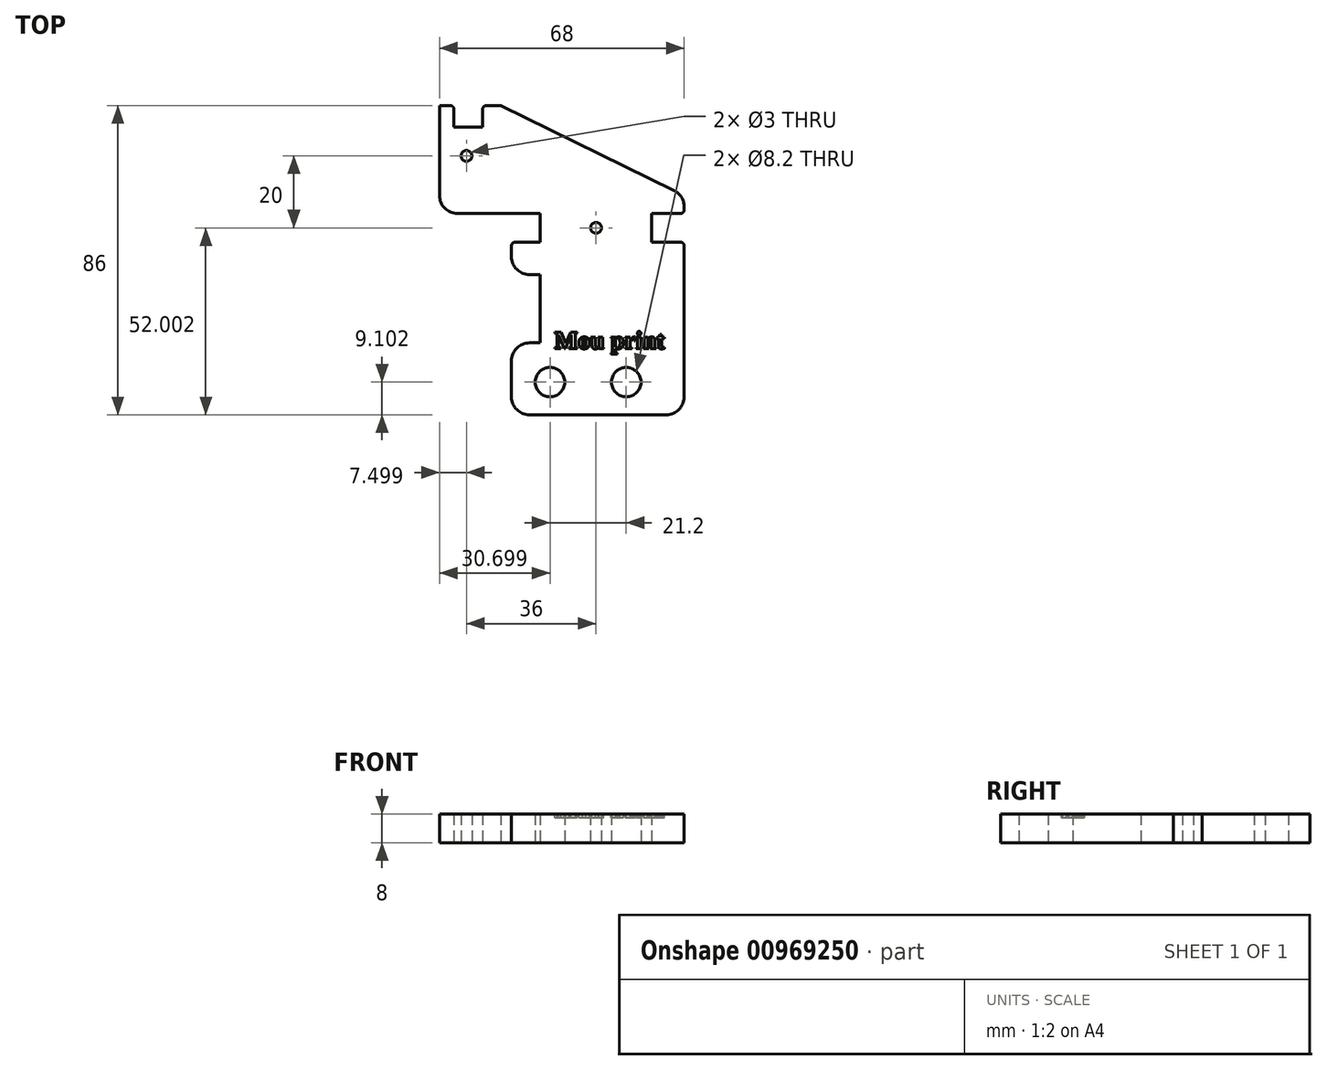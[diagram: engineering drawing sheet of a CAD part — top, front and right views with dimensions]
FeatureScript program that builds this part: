
annotation { "Feature Type Name" : "Feature", "Feature Type Description" : "" }
export const myFeature = defineFeature(function(context is Context, id is Id, definition is map)
    precondition{}
    {
        {
            var Q0;
            Q0=qCreatedBy(makeId("Top.planeOp"),FACE);
            var sketch = newSketch(context, id + "F0", { "sketchPlane" : qUnion([Q0])});
            skLineSegment(sketch, "E0", {"start": v(-27.53, -40.03) * mm, "end": v(10.47, -40.03) * mm});
            skLineSegment(sketch, "E1", {"start": v(-32.53, -35.03) * mm, "end": v(-32.53, -25.03) * mm});
            skLineSegment(sketch, "E2", {"start": v(-27.53, -20.03) * mm, "end": v(-24.53, -20.03) * mm});
            skLineSegment(sketch, "E3", {"start": v(-24.53, -20.03) * mm, "end": v(-24.53, -1.03) * mm});
            skLineSegment(sketch, "E4", {"start": v(-24.53, -1.03) * mm, "end": v(-27.53, -1.03) * mm});
            skLineSegment(sketch, "E5", {"start": v(-32.53, 3.97) * mm, "end": v(-32.53, 7.97) * mm});
            skLineSegment(sketch, "E6", {"start": v(-32.53, 7.97) * mm, "end": v(-24.53, 7.97) * mm});
            skLineSegment(sketch, "E7", {"start": v(-24.53, 7.97) * mm, "end": v(-24.53, 15.97) * mm});
            skLineSegment(sketch, "E8", {"start": v(-24.53, 15.97) * mm, "end": v(-47.53, 15.97) * mm});
            skLineSegment(sketch, "E9", {"start": v(-52.53, 20.97) * mm, "end": v(-52.53, 45.97) * mm});
            skLineSegment(sketch, "E10", {"start": v(-52.53, 45.97) * mm, "end": v(-48.53, 45.97) * mm});
            skLineSegment(sketch, "E11", {"start": v(-48.53, 45.97) * mm, "end": v(-48.53, 39.97) * mm});
            skLineSegment(sketch, "E12", {"start": v(-48.53, 39.97) * mm, "end": v(-40.53, 39.97) * mm});
            skLineSegment(sketch, "E13", {"start": v(-40.53, 39.97) * mm, "end": v(-40.53, 45.97) * mm});
            skLineSegment(sketch, "E14", {"start": v(-40.53, 45.97) * mm, "end": v(-35.53, 45.97) * mm});
            skLineSegment(sketch, "E15", {"start": v(15.47, -35.03) * mm, "end": v(15.47, 7.97) * mm});
            skLineSegment(sketch, "E16", {"start": v(15.47, 7.97) * mm, "end": v(6.47, 7.97) * mm});
            skLineSegment(sketch, "E17", {"start": v(6.47, 7.97) * mm, "end": v(6.47, 15.97) * mm});
            skLineSegment(sketch, "E18", {"start": v(6.47, 15.97) * mm, "end": v(15.47, 15.97) * mm});
            skLineSegment(sketch, "E19", {"start": v(15.47, 15.97) * mm, "end": v(15.47, 17.85) * mm});
            skLineSegment(sketch, "E20", {"start": v(12.67, 22.34) * mm, "end": v(-35.53, 45.97) * mm});
            skCircle(sketch, "E21", {"center": v(-0.63, -30.93) * mm, "radius": 4.1 * mm});
            skCircle(sketch, "E22", {"center": v(-21.83, -30.93) * mm, "radius": 4.1 * mm});
            skPoint(sketch, "E23.visualSharp", {"position": v(-32.53, -40.03) * mm});
            skArc(sketch, "E23.filletArc", {"start": v(-32.53, -35.03) * mm, "mid": v(-31.07, -38.56) * mm, "end": v(-27.53, -40.03) * mm});
            skPoint(sketch, "E24.visualSharp", {"position": v(-52.53, 15.97) * mm});
            skArc(sketch, "E24.filletArc", {"start": v(-52.53, 20.97) * mm, "mid": v(-51.07, 17.44) * mm, "end": v(-47.53, 15.97) * mm});
            skPoint(sketch, "E25.visualSharp", {"position": v(-32.53, -20.03) * mm});
            skArc(sketch, "E25.filletArc", {"start": v(-27.53, -20.03) * mm, "mid": v(-31.07, -21.5) * mm, "end": v(-32.53, -25.03) * mm});
            skPoint(sketch, "E26.visualSharp", {"position": v(15.47, -40.03) * mm});
            skArc(sketch, "E26.filletArc", {"start": v(10.47, -40.03) * mm, "mid": v(14, -38.56) * mm, "end": v(15.47, -35.03) * mm});
            skPoint(sketch, "E27.visualSharp", {"position": v(15.47, 20.97) * mm});
            skArc(sketch, "E27.filletArc", {"start": v(15.47, 17.85) * mm, "mid": v(14.71, 20.5) * mm, "end": v(12.67, 22.34) * mm});
            skPoint(sketch, "E28.visualSharp", {"position": v(-32.53, -1.03) * mm});
            skArc(sketch, "E28.filletArc", {"start": v(-32.53, 3.97) * mm, "mid": v(-31.07, 0.44) * mm, "end": v(-27.53, -1.03) * mm});
            skCircle(sketch, "E29", {"center": v(-9.03, 11.97) * mm, "radius": 1.5 * mm});
            skPoint(sketch, "E29.centerSnap0", {"position": v(-24.53, 11.97) * mm});
            skCircle(sketch, "E30", {"center": v(-45.03, 31.97) * mm, "radius": 1.5 * mm});
            skSolve(sketch);
        }
        {
            var Q0;
            Q0=makeQuery(id+"F0.imprint","IMPRINT",FACE,{"disambiguationData":[TD([[makeQuery(id+"F0.imprint","IMPRINT",EDGE,{"derivedFrom":sQuery(id+"F0.wireOp",EDGE,"E0")}),1.0]])]});
            extrude(context, id + "F1", {"entities" : qUnion([Q0]), "depth" : 8 * mm, "offsetDistance" : 25 * mm});
        }
        {
            var Q0;
            Q0=makeQuery(id+"F1.opExtrude","SWEPT_EDGE",EDGE,{"disambiguationData":[OSD([sQuery(id+"F0.wireOp",EDGE,"E10"),sQuery(id+"F0.wireOp",EDGE,"E11")])]});
            var Q1;
            Q1=makeQuery(id+"F1.opExtrude","SWEPT_EDGE",EDGE,{"disambiguationData":[OSD([sQuery(id+"F0.wireOp",EDGE,"E13"),sQuery(id+"F0.wireOp",EDGE,"E14")])]});
            var Q2;
            Q2=makeQuery(id+"F1.opExtrude","SWEPT_EDGE",EDGE,{"disambiguationData":[OSD([sQuery(id+"F0.wireOp",EDGE,"E18"),sQuery(id+"F0.wireOp",EDGE,"E19")])]});
            var Q3;
            Q3=makeQuery(id+"F1.opExtrude","SWEPT_EDGE",EDGE,{"disambiguationData":[OSD([sQuery(id+"F0.wireOp",EDGE,"E15"),sQuery(id+"F0.wireOp",EDGE,"E16")])]});
            var Q4;
            Q4=makeQuery(id+"F1.opExtrude","SWEPT_EDGE",EDGE,{"disambiguationData":[OSD([sQuery(id+"F0.wireOp",EDGE,"E5"),sQuery(id+"F0.wireOp",EDGE,"E6")])]});
            fillet(context, id + "F2", {"entities" : qUnion([Q0, Q1, Q2, Q3, Q4]), "radius" : 1 * mm, "tangentPropagation" : true, "allowEdgeOverflow" : false});
        }
        {
            var Q0;
            Q0=makeQuery(id+"F1.opExtrude","CAP_FACE",FACE,{"disambiguationData":[OSD([sQuery(id+"F0.wireOp",EDGE,"E0"),sQuery(id+"F0.wireOp",EDGE,"E1"),sQuery(id+"F0.wireOp",EDGE,"E2"),sQuery(id+"F0.wireOp",EDGE,"E3"),sQuery(id+"F0.wireOp",EDGE,"E4"),sQuery(id+"F0.wireOp",EDGE,"E5"),sQuery(id+"F0.wireOp",EDGE,"E6"),sQuery(id+"F0.wireOp",EDGE,"E7"),sQuery(id+"F0.wireOp",EDGE,"E8"),sQuery(id+"F0.wireOp",EDGE,"E9"),sQuery(id+"F0.wireOp",EDGE,"E10"),sQuery(id+"F0.wireOp",EDGE,"E11"),sQuery(id+"F0.wireOp",EDGE,"E12"),sQuery(id+"F0.wireOp",EDGE,"E13"),sQuery(id+"F0.wireOp",EDGE,"E14"),sQuery(id+"F0.wireOp",EDGE,"E15"),sQuery(id+"F0.wireOp",EDGE,"E16"),sQuery(id+"F0.wireOp",EDGE,"E17"),sQuery(id+"F0.wireOp",EDGE,"E18"),sQuery(id+"F0.wireOp",EDGE,"E19"),sQuery(id+"F0.wireOp",EDGE,"E20"),sQuery(id+"F0.wireOp",EDGE,"E21"),sQuery(id+"F0.wireOp",EDGE,"E22"),sQuery(id+"F0.wireOp",EDGE,"E23.filletArc"),sQuery(id+"F0.wireOp",EDGE,"E24.filletArc"),sQuery(id+"F0.wireOp",EDGE,"E25.filletArc"),sQuery(id+"F0.wireOp",EDGE,"E26.filletArc"),sQuery(id+"F0.wireOp",EDGE,"E27.filletArc"),sQuery(id+"F0.wireOp",EDGE,"E28.filletArc"),sQuery(id+"F0.wireOp",EDGE,"E29"),sQuery(id+"F0.wireOp",EDGE,"E30")])],"isStart":false});
            var sketch = newSketch(context, id + "F3", { "sketchPlane" : qUnion([Q0])});
            skText(sketch, "E31", { "text": "Mou print", "fontName": "Tinos-Bold.ttf"});
            const initialGuessF3  = {"E31": [-0.0206, -0.02163, 1, 0, 0.005]};
            skSetInitialGuess(sketch, initialGuessF3);
            skSolve(sketch);
        }
        {
            var Q0;
            Q0 = qSketchRegion(id + "F3", true);
            extrude(context, id + "F4", {"entities" : qUnion([Q0]), "operationType" : NewBodyOperationType.REMOVE, "oppositeDirection" : true, "depth" : 1 * mm, "offsetDistance" : 25 * mm});
        }
    });
